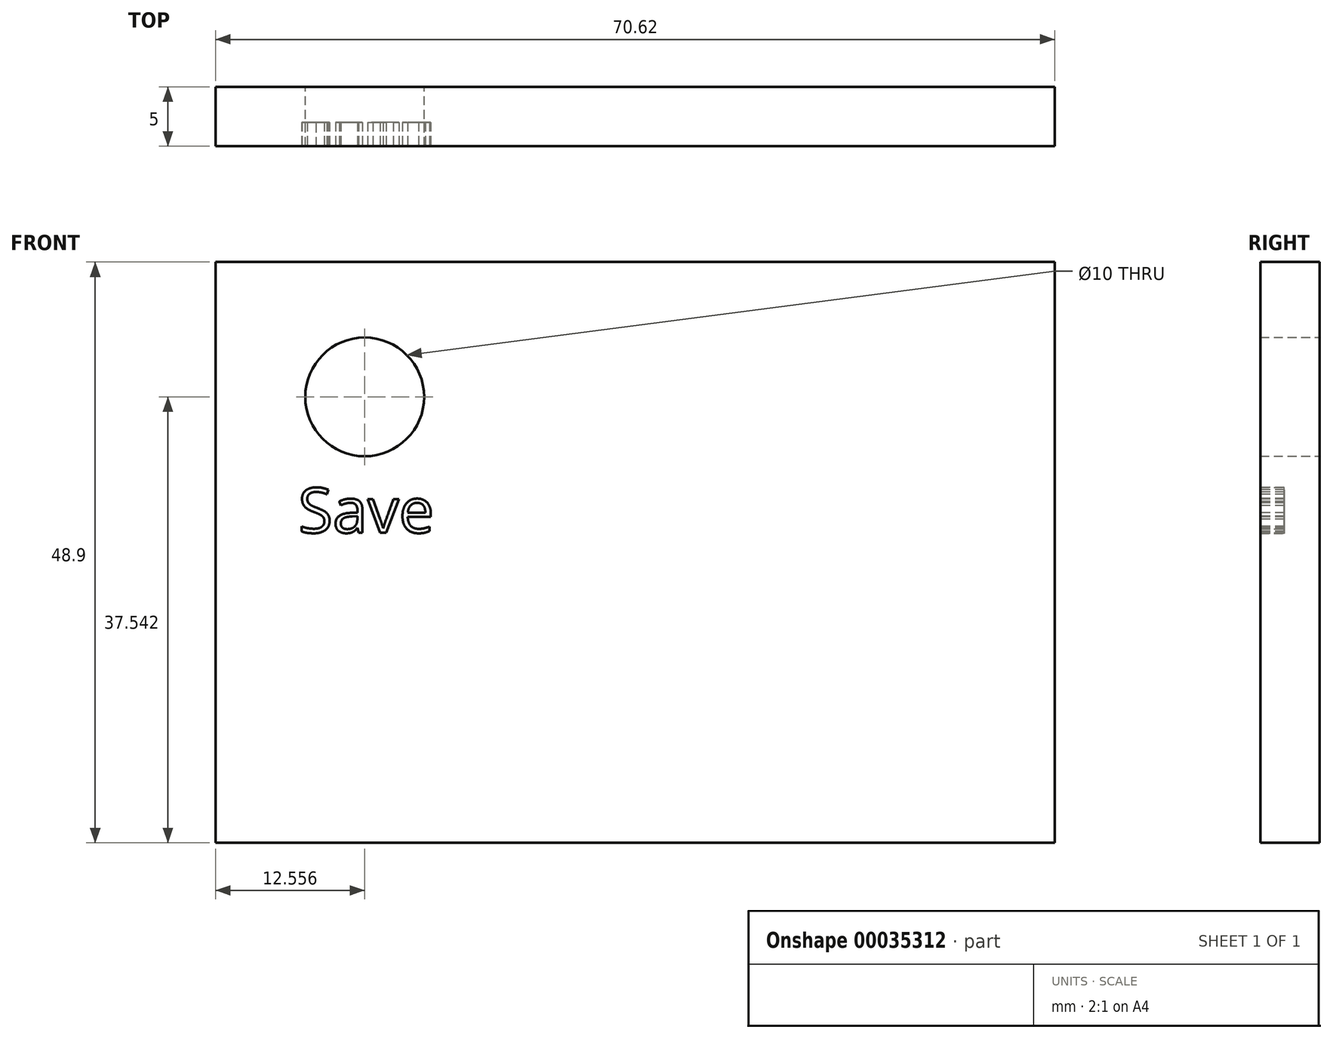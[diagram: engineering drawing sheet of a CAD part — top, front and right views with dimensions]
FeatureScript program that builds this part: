
annotation { "Feature Type Name" : "Feature", "Feature Type Description" : "" }
export const myFeature = defineFeature(function(context is Context, id is Id, definition is map)
    precondition{}
    {
        {
            var Q0;
            Q0=qCreatedBy(makeId("Front.planeOp"),FACE);
            var sketch = newSketch(context, id + "F0", { "sketchPlane" : qUnion([Q0])});
            skLineSegment(sketch, "E0.bottom", {"start": v(0, 0) * mm, "end": v(70.62, 0) * mm});
            skLineSegment(sketch, "E0.top", {"start": v(0, 48.9) * mm, "end": v(70.62, 48.9) * mm});
            skLineSegment(sketch, "E0.left", {"start": v(0, 0) * mm, "end": v(0, 48.9) * mm});
            skLineSegment(sketch, "E0.right", {"start": v(70.62, 0) * mm, "end": v(70.62, 48.9) * mm});
            skCircle(sketch, "E1", {"center": v(12.56, 37.54) * mm, "radius": 5 * mm});
            skSolve(sketch);
        }
        {
            var Q0;
            Q0=makeQuery(id+"F0.imprint","IMPRINT",FACE,{"disambiguationData":[TD([[makeQuery(id+"F0.imprint","IMPRINT",EDGE,{"derivedFrom":sQuery(id+"F0.wireOp",EDGE,"E0.bottom")}),1.0]])]});
            extrude(context, id + "F1", {"entities" : qUnion([Q0]), "depth" : 5 * mm});
        }
        {
            var Q0;
            Q0=makeQuery(id+"F0.imprint","IMPRINT",FACE,{"disambiguationData":[TD([[makeQuery(id+"F0.imprint","IMPRINT",EDGE,{"derivedFrom":sQuery(id+"F0.wireOp",EDGE,"E1")}),1.0]])]});
            extrude(context, id + "F2", {"entities" : qUnion([Q0]), "operationType" : NewBodyOperationType.REMOVE, "endBound" : BoundingType.THROUGH_ALL, "depth" : 25.4 * mm});
        }
        {
            var Q0;
            Q0=makeQuery(id+"F1.opExtrude","CAP_FACE",FACE,{"disambiguationData":[OSD([sQuery(id+"F0.wireOp",EDGE,"E0.bottom"),sQuery(id+"F0.wireOp",EDGE,"E0.top"),sQuery(id+"F0.wireOp",EDGE,"E0.left"),sQuery(id+"F0.wireOp",EDGE,"E0.right"),sQuery(id+"F0.wireOp",EDGE,"E1")])],"isStart":false});
            var sketch = newSketch(context, id + "F3", { "sketchPlane" : qUnion([Q0])});
            skText(sketch, "E2", { "text": "Save", "fontName": "OpenSans-Regular.ttf"});
            const initialGuessF3  = {"E2": [0.00696, 0.02611, 1, 0, 0.0038]};
            skSetInitialGuess(sketch, initialGuessF3);
            skSolve(sketch);
        }
        {
            var Q0;
            Q0 = qSketchRegion(id + "F3", true);
            extrude(context, id + "F4", {"entities" : qUnion([Q0]), "operationType" : NewBodyOperationType.REMOVE, "oppositeDirection" : true, "depth" : 2 * mm});
        }
    });
